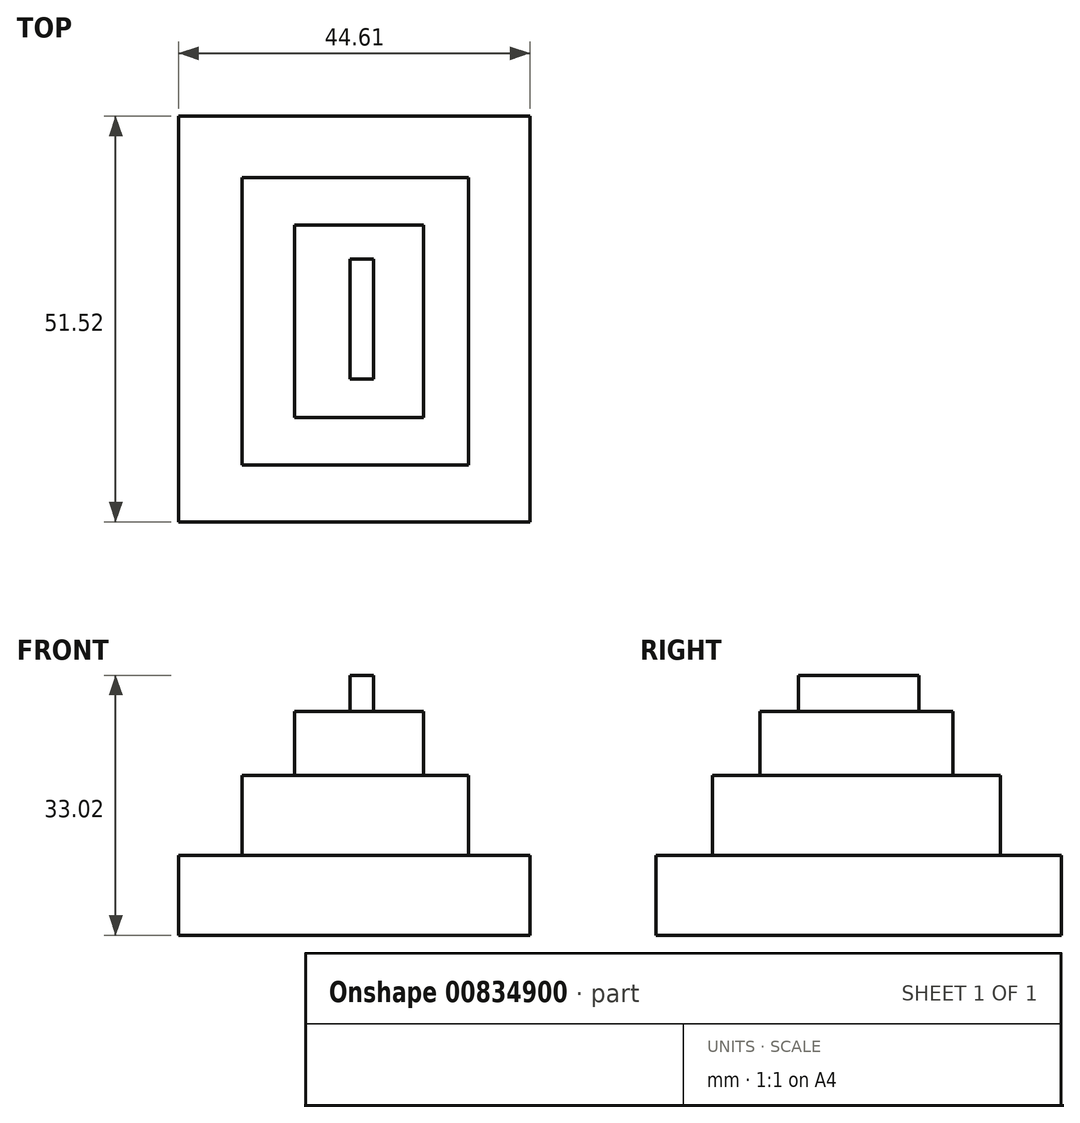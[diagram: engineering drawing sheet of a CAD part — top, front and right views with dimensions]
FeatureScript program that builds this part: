
annotation { "Feature Type Name" : "Feature", "Feature Type Description" : "" }
export const myFeature = defineFeature(function(context is Context, id is Id, definition is map)
    precondition{}
    {
        {
            var Q0;
            Q0=qCreatedBy(makeId("Top.planeOp"),FACE);
            var sketch = newSketch(context, id + "F0", { "sketchPlane" : qUnion([Q0])});
            skLineSegment(sketch, "E0.bottom", {"start": v(-21.73, 27.2) * mm, "end": v(22.88, 27.2) * mm});
            skLineSegment(sketch, "E0.top", {"start": v(-21.73, -24.32) * mm, "end": v(22.88, -24.32) * mm});
            skLineSegment(sketch, "E0.left", {"start": v(-21.73, 27.2) * mm, "end": v(-21.73, -24.32) * mm});
            skLineSegment(sketch, "E0.right", {"start": v(22.88, 27.2) * mm, "end": v(22.88, -24.32) * mm});
            skSolve(sketch);
        }
        {
            var Q0;
            Q0 = qSketchRegion(id + "F0", true);
            extrude(context, id + "F1", {"entities" : qUnion([Q0]), "depth" : 10.16 * mm, "offsetDistance" : 25.4 * mm});
        }
        {
            var Q0;
            Q0=qCreatedBy(makeId("Top.planeOp"),FACE);
            var sketch = newSketch(context, id + "F2", { "sketchPlane" : qUnion([Q0])});
            skLineSegment(sketch, "E1.bottom", {"start": v(-13.67, 19.43) * mm, "end": v(15.1, 19.43) * mm});
            skLineSegment(sketch, "E1.top", {"start": v(-13.67, -17.12) * mm, "end": v(15.1, -17.12) * mm});
            skLineSegment(sketch, "E1.left", {"start": v(-13.67, 19.43) * mm, "end": v(-13.67, -17.12) * mm});
            skLineSegment(sketch, "E1.right", {"start": v(15.1, 19.43) * mm, "end": v(15.1, -17.12) * mm});
            skSolve(sketch);
        }
        {
            var Q0;
            Q0 = qSketchRegion(id + "F2", true);
            extrude(context, id + "F3", {"entities" : qUnion([Q0]), "operationType" : NewBodyOperationType.ADD, "depth" : 20.32 * mm, "offsetDistance" : 25.4 * mm});
        }
        {
            var Q0;
            Q0=qCreatedBy(makeId("Top.planeOp"),FACE);
            var sketch = newSketch(context, id + "F4", { "sketchPlane" : qUnion([Q0])});
            skLineSegment(sketch, "E2.bottom", {"start": v(-7.05, 13.38) * mm, "end": v(9.35, 13.38) * mm});
            skLineSegment(sketch, "E2.top", {"start": v(-7.05, -11.08) * mm, "end": v(9.35, -11.08) * mm});
            skLineSegment(sketch, "E2.left", {"start": v(-7.05, 13.38) * mm, "end": v(-7.05, -11.08) * mm});
            skLineSegment(sketch, "E2.right", {"start": v(9.35, 13.38) * mm, "end": v(9.35, -11.08) * mm});
            skSolve(sketch);
        }
        {
            var Q0;
            Q0 = qSketchRegion(id + "F4", true);
            extrude(context, id + "F5", {"entities" : qUnion([Q0]), "operationType" : NewBodyOperationType.ADD, "depth" : 28.45 * mm, "offsetDistance" : 25.4 * mm});
        }
        {
            var Q0;
            Q0=qCreatedBy(makeId("Top.planeOp"),FACE);
            var sketch = newSketch(context, id + "F6", { "sketchPlane" : qUnion([Q0])});
            skLineSegment(sketch, "E3.bottom", {"start": v(0, 9.07) * mm, "end": v(3.02, 9.07) * mm});
            skLineSegment(sketch, "E3.top", {"start": v(0, -6.19) * mm, "end": v(3.02, -6.19) * mm});
            skLineSegment(sketch, "E3.left", {"start": v(0, 9.07) * mm, "end": v(0, -6.19) * mm});
            skLineSegment(sketch, "E3.right", {"start": v(3.02, 9.07) * mm, "end": v(3.02, -6.19) * mm});
            skSolve(sketch);
        }
        {
            var Q0;
            Q0 = qSketchRegion(id + "F6", true);
            extrude(context, id + "F7", {"entities" : qUnion([Q0]), "operationType" : NewBodyOperationType.ADD, "depth" : 33.02 * mm, "offsetDistance" : 25.4 * mm});
        }
    });
